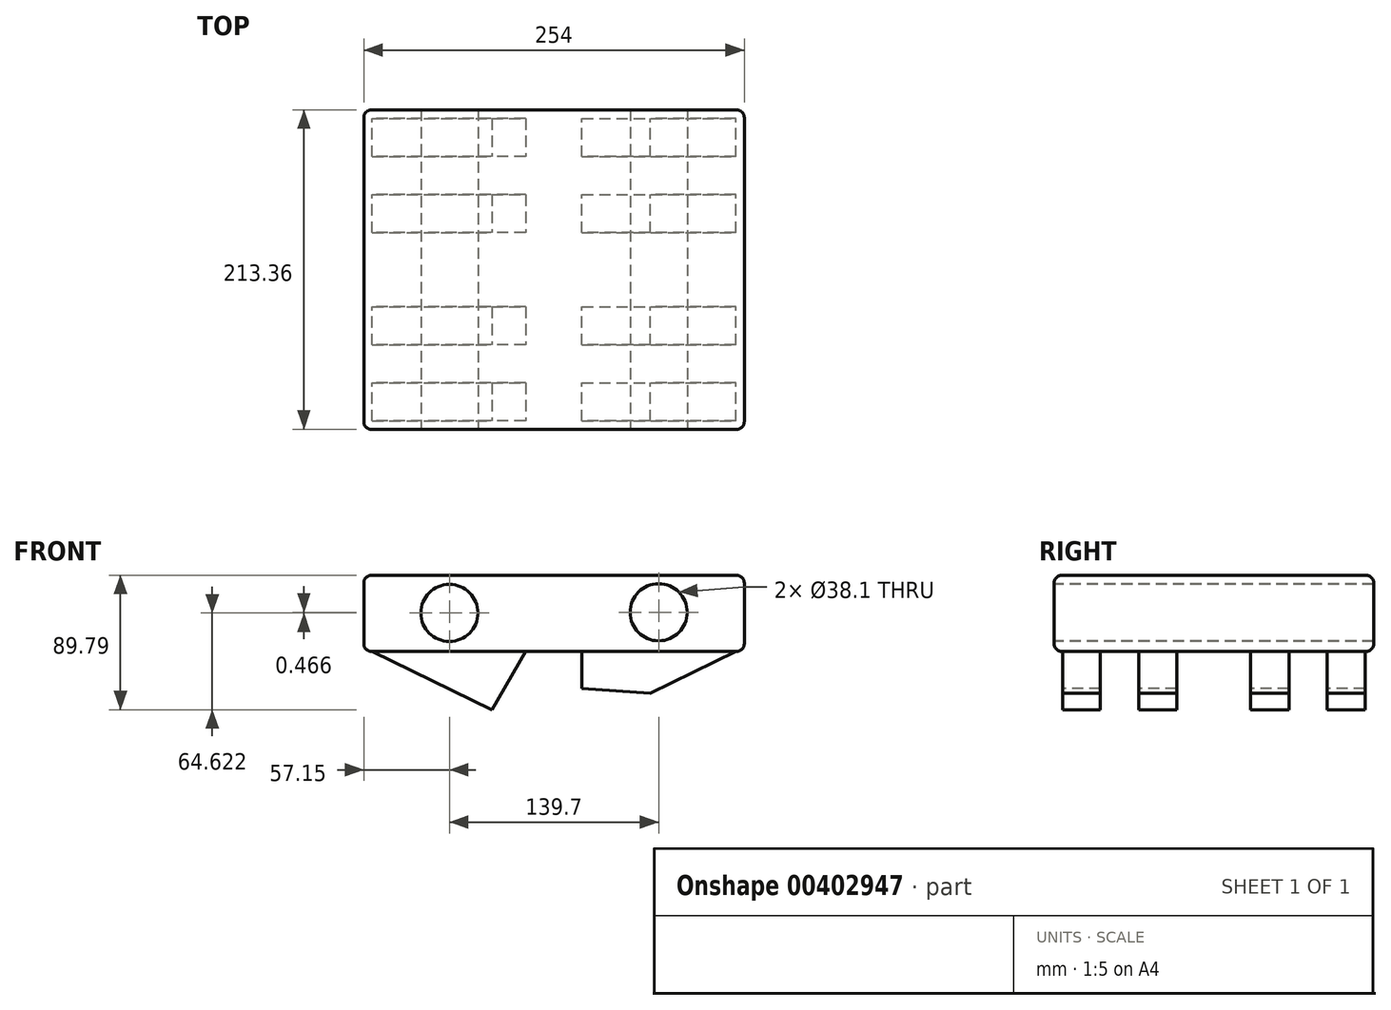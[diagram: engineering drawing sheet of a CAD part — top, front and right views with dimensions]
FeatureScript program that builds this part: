
annotation { "Feature Type Name" : "Feature", "Feature Type Description" : "" }
export const myFeature = defineFeature(function(context is Context, id is Id, definition is map)
    precondition{}
    {
        {
            var Q0;
            Q0=qCreatedBy(makeId("Front.planeOp"),FACE);
            var sketch = newSketch(context, id + "F0", { "sketchPlane" : qUnion([Q0])});
            skLineSegment(sketch, "E0.bottom", {"start": v(127, 25.4) * mm, "end": v(-127, 25.4) * mm});
            skLineSegment(sketch, "E0.top", {"start": v(127, -25.4) * mm, "end": v(-127, -25.4) * mm});
            skLineSegment(sketch, "E0.left", {"start": v(127, 25.4) * mm, "end": v(127, -25.4) * mm});
            skLineSegment(sketch, "E0.right", {"start": v(-127, 25.4) * mm, "end": v(-127, -25.4) * mm});
            skPoint(sketch, "E0.middle", {"position": v(0, 0) * mm});
            skCircle(sketch, "E1", {"center": v(-69.85, 0.23) * mm, "radius": 19.05 * mm});
            skCircle(sketch, "E2", {"center": v(69.85, 0.7) * mm, "radius": 19.05 * mm});
            skSolve(sketch);
        }
        {
            var Q0;
            Q0=makeQuery(id+"F0.imprint","IMPRINT",FACE,{"disambiguationData":[TD([[makeQuery(id+"F0.imprint","IMPRINT",EDGE,{"derivedFrom":sQuery(id+"F0.wireOp",EDGE,"E0.bottom")}),1.0]])]});
            extrude(context, id + "F1", {"entities" : qUnion([Q0]), "endBound" : BoundingType.SYMMETRIC, "oppositeDirection" : true, "depth" : 213.36 * mm});
        }
        {
            var Q0;
            Q0=makeQuery(id+"F1.opExtrude","CAP_EDGE",EDGE,{"disambiguationData":[OSD([sQuery(id+"F0.wireOp",EDGE,"E0.right")])],"isStart":true});
            var Q1;
            Q1=makeQuery(id+"F1.opExtrude","CAP_EDGE",EDGE,{"disambiguationData":[OSD([sQuery(id+"F0.wireOp",EDGE,"E0.left")])],"isStart":true});
            var Q2;
            Q2=makeQuery(id+"F1.opExtrude","CAP_EDGE",EDGE,{"disambiguationData":[OSD([sQuery(id+"F0.wireOp",EDGE,"E0.left")])],"isStart":false});
            var Q3;
            Q3=makeQuery(id+"F1.opExtrude","CAP_EDGE",EDGE,{"disambiguationData":[OSD([sQuery(id+"F0.wireOp",EDGE,"E0.right")])],"isStart":false});
            var Q4;
            Q4=makeQuery(id+"F1.opExtrude","CAP_EDGE",EDGE,{"disambiguationData":[OSD([sQuery(id+"F0.wireOp",EDGE,"E0.bottom")])],"isStart":false});
            var Q5;
            Q5=makeQuery(id+"F1.opExtrude","CAP_EDGE",EDGE,{"disambiguationData":[OSD([sQuery(id+"F0.wireOp",EDGE,"E0.top")])],"isStart":false});
            var Q6;
            Q6=makeQuery(id+"F1.opExtrude","SWEPT_EDGE",EDGE,{"disambiguationData":[OSD([sQuery(id+"F0.wireOp",EDGE,"E0.bottom"),sQuery(id+"F0.wireOp",EDGE,"E0.right")])]});
            var Q7;
            Q7=makeQuery(id+"F1.opExtrude","SWEPT_EDGE",EDGE,{"disambiguationData":[OSD([sQuery(id+"F0.wireOp",EDGE,"E0.bottom"),sQuery(id+"F0.wireOp",EDGE,"E0.left")])]});
            var Q8;
            Q8=makeQuery(id+"F1.opExtrude","CAP_EDGE",EDGE,{"disambiguationData":[OSD([sQuery(id+"F0.wireOp",EDGE,"E0.top")])],"isStart":true});
            fillet(context, id + "F2", {"entities" : qUnion([Q0, Q1, Q2, Q3, Q4, Q5, Q6, Q7, Q8]), "radius" : 5.08 * mm, "tangentPropagation" : true, "allowEdgeOverflow" : false});
        }
        {
            var Q0;
            Q0=makeQuery(id+"F1.opExtrude","SWEPT_EDGE",EDGE,{"disambiguationData":[OSD([sQuery(id+"F0.wireOp",EDGE,"E0.top"),sQuery(id+"F0.wireOp",EDGE,"E0.right")])]});
            var Q1;
            Q1=makeQuery(id+"F1.opExtrude","SWEPT_EDGE",EDGE,{"disambiguationData":[OSD([sQuery(id+"F0.wireOp",EDGE,"E0.top"),sQuery(id+"F0.wireOp",EDGE,"E0.left")])]});
            fillet(context, id + "F3", {"entities" : qUnion([Q0, Q1]), "radius" : 5.08 * mm, "tangentPropagation" : true, "allowEdgeOverflow" : false});
        }
        {
            var Q0;
            Q0=makeQuery(id+"F1.opExtrude","CAP_EDGE",EDGE,{"disambiguationData":[OSD([sQuery(id+"F0.wireOp",EDGE,"E0.bottom")])],"isStart":true});
            fillet(context, id + "F4", {"entities" : qUnion([Q0]), "radius" : 5.08 * mm, "tangentPropagation" : true, "allowEdgeOverflow" : false});
        }
        {
            var Q0;
            Q0=qCreatedBy(makeId("Front.planeOp"),FACE);
            var sketch = newSketch(context, id + "F5", { "sketchPlane" : qUnion([Q0])});
            skLineSegment(sketch, "E3", {"start": v(123.92, -25.94) * mm, "end": v(21.2, -76.06) * mm});
            skLineSegment(sketch, "E4", {"start": v(21.2, -76.06) * mm, "end": v(21.2, -25.94) * mm});
            skLineSegment(sketch, "E5", {"start": v(21.2, -25.94) * mm, "end": v(123.92, -25.94) * mm});
            skSolve(sketch);
        }
        {
            var Q0;
            Q0=makeQuery(id+"F5.imprint","IMPRINT",FACE,{"disambiguationData":[TD([[makeQuery(id+"F5.imprint","IMPRINT",EDGE,{"derivedFrom":sQuery(id+"F5.wireOp",EDGE,"E3")}),-1.0]])]});
            extrude(context, id + "F6", {"entities" : qUnion([Q0]), "depth" : 25.4 * mm});
        }
        {
            var Q0;
            Q0=makeQuery(id+"F6.opExtrude","SWEPT_BODY",BODY,{"disambiguationData":[OSD([sQuery(id+"F5.wireOp",EDGE,"E3"),sQuery(id+"F5.wireOp",EDGE,"E4"),sQuery(id+"F5.wireOp",EDGE,"E5")])]});
            transform(context, id + "F7", {"entities" : qUnion([Q0]), "transformType" : TransformType.TRANSLATION_3D, "dx" : -2.54 * mm, "dy" : -75.95 * mm, "dz" : -17.27 * mm, "makeCopy" : false});
        }
        {
            var Q0;
            Q0=makeQuery(id+"F6.opExtrude","SWEPT_BODY",BODY,{"disambiguationData":[OSD([sQuery(id+"F5.wireOp",EDGE,"E3"),sQuery(id+"F5.wireOp",EDGE,"E4"),sQuery(id+"F5.wireOp",EDGE,"E5")])]});
            var Q1;
            Q1=makeQuery(id+"F6.opExtrude","SWEPT_EDGE",EDGE,{"disambiguationData":[OSD([sQuery(id+"F5.wireOp",EDGE,"E3"),sQuery(id+"F5.wireOp",EDGE,"E4")])]});
            var Q2;
            Q2=makeQuery(id+"F6.opExtrude","SWEPT_EDGE",EDGE,{"disambiguationData":[OSD([sQuery(id+"F5.wireOp",EDGE,"E3"),sQuery(id+"F5.wireOp",EDGE,"E4")])]});
            transform(context, id + "F8", {"entities" : qUnion([Q0]), "transformType" : TransformType.TRANSLATION_DISTANCE, "transformDirection" : qUnion([Q2]), "distance" : 50.8 * mm, "makeCopy" : true});
        }
        {
            var Q0;
            Q0=makeQuery(id+"F8.opPattern","COPY",BODY,{"derivedFrom":makeQuery(id+"F6.opExtrude","SWEPT_BODY",BODY,{"disambiguationData":[OSD([sQuery(id+"F5.wireOp",EDGE,"E3"),sQuery(id+"F5.wireOp",EDGE,"E4"),sQuery(id+"F5.wireOp",EDGE,"E5")])]}),"instanceName":"1"});
            var Q1;
            Q1=makeQuery(id+"F6.opExtrude","SWEPT_BODY",BODY,{"disambiguationData":[OSD([sQuery(id+"F5.wireOp",EDGE,"E3"),sQuery(id+"F5.wireOp",EDGE,"E4"),sQuery(id+"F5.wireOp",EDGE,"E5")])]});
            transform(context, id + "F9", {"entities" : qUnion([Q0, Q1]), "transformType" : TransformType.TRANSLATION_3D, "dx" : 0 * mm, "dy" : 125.98 * mm, "dz" : 0 * mm, "makeCopy" : false});
        }
        {
            var Q0;
            Q0=makeQuery(id+"F6.opExtrude","SWEPT_BODY",BODY,{"disambiguationData":[OSD([sQuery(id+"F5.wireOp",EDGE,"E3"),sQuery(id+"F5.wireOp",EDGE,"E4"),sQuery(id+"F5.wireOp",EDGE,"E5")])]});
            var Q1;
            Q1=makeQuery(id+"F8.opPattern","COPY",BODY,{"derivedFrom":makeQuery(id+"F6.opExtrude","SWEPT_BODY",BODY,{"disambiguationData":[OSD([sQuery(id+"F5.wireOp",EDGE,"E3"),sQuery(id+"F5.wireOp",EDGE,"E4"),sQuery(id+"F5.wireOp",EDGE,"E5")])]}),"instanceName":"1"});
            transform(context, id + "F10", {"entities" : qUnion([Q0, Q1]), "transformType" : TransformType.TRANSLATION_3D, "dx" : 0 * mm, "dy" : -125.73 * mm, "dz" : 0 * mm, "makeCopy" : true});
        }
        {
            var Q0;
            Q0=makeQuery(id+"F10.opPattern","COPY",BODY,{"derivedFrom":makeQuery(id+"F6.opExtrude","SWEPT_BODY",BODY,{"disambiguationData":[OSD([sQuery(id+"F5.wireOp",EDGE,"E3"),sQuery(id+"F5.wireOp",EDGE,"E4"),sQuery(id+"F5.wireOp",EDGE,"E5")])]}),"instanceName":"1"});
            var Q1;
            Q1=makeQuery(id+"F10.opPattern","COPY",BODY,{"derivedFrom":makeQuery(id+"F8.opPattern","COPY",BODY,{"derivedFrom":makeQuery(id+"F6.opExtrude","SWEPT_BODY",BODY,{"disambiguationData":[OSD([sQuery(id+"F5.wireOp",EDGE,"E3"),sQuery(id+"F5.wireOp",EDGE,"E4"),sQuery(id+"F5.wireOp",EDGE,"E5")])]}),"instanceName":"1"}),"instanceName":"1"});
            var Q2;
            Q2=makeQuery(id+"F6.opExtrude","SWEPT_BODY",BODY,{"disambiguationData":[OSD([sQuery(id+"F5.wireOp",EDGE,"E3"),sQuery(id+"F5.wireOp",EDGE,"E4"),sQuery(id+"F5.wireOp",EDGE,"E5")])]});
            var Q3;
            Q3=makeQuery(id+"F8.opPattern","COPY",BODY,{"derivedFrom":makeQuery(id+"F6.opExtrude","SWEPT_BODY",BODY,{"disambiguationData":[OSD([sQuery(id+"F5.wireOp",EDGE,"E3"),sQuery(id+"F5.wireOp",EDGE,"E4"),sQuery(id+"F5.wireOp",EDGE,"E5")])]}),"instanceName":"1"});
            var Q4;
            Q4=qCreatedBy(makeId("Right.planeOp"),FACE);
            mirror(context, id + "F11", {"entities" : qUnion([Q0, Q1, Q2, Q3]), "mirrorPlane" : qUnion([Q4])});
        }
        {
            var Q0;
            Q0=makeQuery(id+"F11.opPattern","COPY",BODY,{"derivedFrom":makeQuery(id+"F10.opPattern","COPY",BODY,{"derivedFrom":makeQuery(id+"F6.opExtrude","SWEPT_BODY",BODY,{"disambiguationData":[OSD([sQuery(id+"F5.wireOp",EDGE,"E3"),sQuery(id+"F5.wireOp",EDGE,"E4"),sQuery(id+"F5.wireOp",EDGE,"E5")])]}),"instanceName":"1"}),"instanceName":"1"});
            var Q1;
            Q1=makeQuery(id+"F11.opPattern","COPY",BODY,{"derivedFrom":makeQuery(id+"F10.opPattern","COPY",BODY,{"derivedFrom":makeQuery(id+"F8.opPattern","COPY",BODY,{"derivedFrom":makeQuery(id+"F6.opExtrude","SWEPT_BODY",BODY,{"disambiguationData":[OSD([sQuery(id+"F5.wireOp",EDGE,"E3"),sQuery(id+"F5.wireOp",EDGE,"E4"),sQuery(id+"F5.wireOp",EDGE,"E5")])]}),"instanceName":"1"}),"instanceName":"1"}),"instanceName":"1"});
            var Q2;
            Q2=makeQuery(id+"F11.opPattern","COPY",BODY,{"derivedFrom":makeQuery(id+"F6.opExtrude","SWEPT_BODY",BODY,{"disambiguationData":[OSD([sQuery(id+"F5.wireOp",EDGE,"E3"),sQuery(id+"F5.wireOp",EDGE,"E4"),sQuery(id+"F5.wireOp",EDGE,"E5")])]}),"instanceName":"1"});
            var Q3;
            Q3=makeQuery(id+"F11.opPattern","COPY",BODY,{"derivedFrom":makeQuery(id+"F8.opPattern","COPY",BODY,{"derivedFrom":makeQuery(id+"F6.opExtrude","SWEPT_BODY",BODY,{"disambiguationData":[OSD([sQuery(id+"F5.wireOp",EDGE,"E3"),sQuery(id+"F5.wireOp",EDGE,"E4"),sQuery(id+"F5.wireOp",EDGE,"E5")])]}),"instanceName":"1"}),"instanceName":"1"});
            var Q4;
            Q4=makeQuery(id+"F8.opPattern","COPY",BODY,{"derivedFrom":makeQuery(id+"F6.opExtrude","SWEPT_BODY",BODY,{"disambiguationData":[OSD([sQuery(id+"F5.wireOp",EDGE,"E3"),sQuery(id+"F5.wireOp",EDGE,"E4"),sQuery(id+"F5.wireOp",EDGE,"E5")])]}),"instanceName":"1"});
            var Q5;
            Q5=makeQuery(id+"F6.opExtrude","SWEPT_BODY",BODY,{"disambiguationData":[OSD([sQuery(id+"F5.wireOp",EDGE,"E3"),sQuery(id+"F5.wireOp",EDGE,"E4"),sQuery(id+"F5.wireOp",EDGE,"E5")])]});
            var Q6;
            Q6=makeQuery(id+"F10.opPattern","COPY",BODY,{"derivedFrom":makeQuery(id+"F8.opPattern","COPY",BODY,{"derivedFrom":makeQuery(id+"F6.opExtrude","SWEPT_BODY",BODY,{"disambiguationData":[OSD([sQuery(id+"F5.wireOp",EDGE,"E3"),sQuery(id+"F5.wireOp",EDGE,"E4"),sQuery(id+"F5.wireOp",EDGE,"E5")])]}),"instanceName":"1"}),"instanceName":"1"});
            var Q7;
            Q7=makeQuery(id+"F10.opPattern","COPY",BODY,{"derivedFrom":makeQuery(id+"F6.opExtrude","SWEPT_BODY",BODY,{"disambiguationData":[OSD([sQuery(id+"F5.wireOp",EDGE,"E3"),sQuery(id+"F5.wireOp",EDGE,"E4"),sQuery(id+"F5.wireOp",EDGE,"E5")])]}),"instanceName":"1"});
            transform(context, id + "F12", {"entities" : qUnion([Q0, Q1, Q2, Q3, Q4, Q5, Q6, Q7]), "transformType" : TransformType.TRANSLATION_3D, "dx" : 0 * mm, "dy" : 0 * mm, "dz" : 17.78 * mm, "makeCopy" : false});
        }
        {
            var Q0;
            Q0=makeQuery(id+"F11.opPattern","COPY",EDGE,{"derivedFrom":makeQuery(id+"F8.opPattern","COPY",EDGE,{"derivedFrom":makeQuery(id+"F6.opExtrude","SWEPT_EDGE",EDGE,{"disambiguationData":[OSD([sQuery(id+"F5.wireOp",EDGE,"E3"),sQuery(id+"F5.wireOp",EDGE,"E4")])]}),"instanceName":"1"}),"instanceName":"1"});
            var Q1;
            Q1=makeQuery(id+"F8.opPattern","COPY",EDGE,{"derivedFrom":makeQuery(id+"F6.opExtrude","SWEPT_EDGE",EDGE,{"disambiguationData":[OSD([sQuery(id+"F5.wireOp",EDGE,"E3"),sQuery(id+"F5.wireOp",EDGE,"E4")])]}),"instanceName":"1"});
            var Q2;
            Q2=makeQuery(id+"F6.opExtrude","SWEPT_EDGE",EDGE,{"disambiguationData":[OSD([sQuery(id+"F5.wireOp",EDGE,"E3"),sQuery(id+"F5.wireOp",EDGE,"E4")])]});
            var Q3;
            Q3=makeQuery(id+"F11.opPattern","COPY",EDGE,{"derivedFrom":makeQuery(id+"F6.opExtrude","SWEPT_EDGE",EDGE,{"disambiguationData":[OSD([sQuery(id+"F5.wireOp",EDGE,"E3"),sQuery(id+"F5.wireOp",EDGE,"E4")])]}),"instanceName":"1"});
            var Q4;
            Q4=makeQuery(id+"F11.opPattern","COPY",EDGE,{"derivedFrom":makeQuery(id+"F10.opPattern","COPY",EDGE,{"derivedFrom":makeQuery(id+"F8.opPattern","COPY",EDGE,{"derivedFrom":makeQuery(id+"F6.opExtrude","SWEPT_EDGE",EDGE,{"disambiguationData":[OSD([sQuery(id+"F5.wireOp",EDGE,"E3"),sQuery(id+"F5.wireOp",EDGE,"E4")])]}),"instanceName":"1"}),"instanceName":"1"}),"instanceName":"1"});
            var Q5;
            Q5=makeQuery(id+"F10.opPattern","COPY",EDGE,{"derivedFrom":makeQuery(id+"F8.opPattern","COPY",EDGE,{"derivedFrom":makeQuery(id+"F6.opExtrude","SWEPT_EDGE",EDGE,{"disambiguationData":[OSD([sQuery(id+"F5.wireOp",EDGE,"E3"),sQuery(id+"F5.wireOp",EDGE,"E4")])]}),"instanceName":"1"}),"instanceName":"1"});
            var Q6;
            Q6=makeQuery(id+"F10.opPattern","COPY",EDGE,{"derivedFrom":makeQuery(id+"F6.opExtrude","SWEPT_EDGE",EDGE,{"disambiguationData":[OSD([sQuery(id+"F5.wireOp",EDGE,"E3"),sQuery(id+"F5.wireOp",EDGE,"E4")])]}),"instanceName":"1"});
            var Q7;
            Q7=makeQuery(id+"F11.opPattern","COPY",EDGE,{"derivedFrom":makeQuery(id+"F10.opPattern","COPY",EDGE,{"derivedFrom":makeQuery(id+"F6.opExtrude","SWEPT_EDGE",EDGE,{"disambiguationData":[OSD([sQuery(id+"F5.wireOp",EDGE,"E3"),sQuery(id+"F5.wireOp",EDGE,"E4")])]}),"instanceName":"1"}),"instanceName":"1"});
            chamfer(context, id + "F13", {"entities" : qUnion([Q0, Q1, Q2, Q3, Q4, Q5, Q6, Q7]), "chamferType" : ChamferType.OFFSET_ANGLE, "width" : 50.8 * mm, "oppositeDirection" : false, "angle" : 30 * degree, "tangentPropagation" : true});
        }
    });
